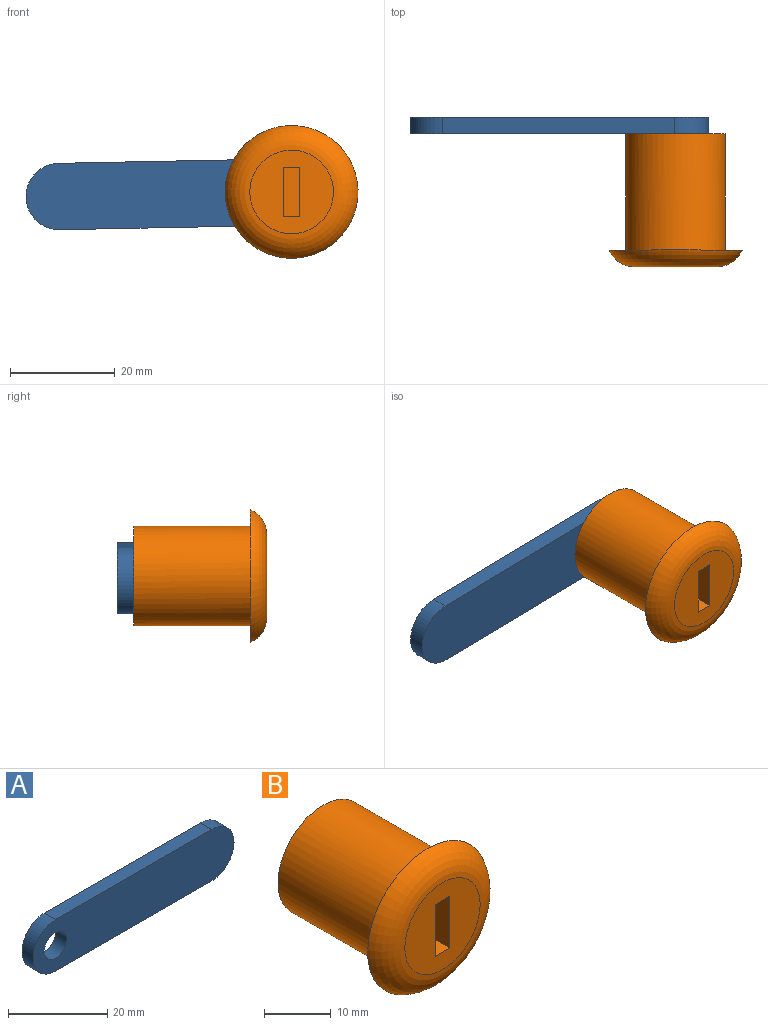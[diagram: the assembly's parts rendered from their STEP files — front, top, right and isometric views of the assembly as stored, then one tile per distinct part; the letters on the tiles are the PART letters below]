
ASSEMBLY  parts=2 mates=1
PART A: 7 faces, bbox 57.2x3.2x12.7 mm
  f0: plane 44.45x3.18mm, normal (0,0,-1), area 141.1mm2, adj f1,f4,f5,f6
  f1: cylinder r=6.35mm len=12.7mm, axis (0,1,0), area 63.3mm2, adj f0,f2,f5,f6
  f2: plane 44.45x3.18mm, normal (0,0,1), area 141.1mm2, adj f1,f4,f5,f6
  f3: cylinder r=3.17mm len=6.35mm, axis (0,1,0), area 63.3mm2, adj f5,f6
  f4: cylinder r=6.35mm len=12.7mm, axis (0,1,0), area 63.3mm2, adj f0,f2,f5,f6
  f5: plane 57.15x12.7mm, normal (0,-1,0), area 659.5mm2, adj f0,f1,f2,f3,f4
  f6: plane 57.15x12.7mm, normal (0,1,0), area 659.5mm2, adj f0,f1,f2,f3,f4
PART B: 10 faces, bbox 28.3x25.4x28.3 mm
  f0: plane 15.98x15.98mm, normal (0,-1,0), area 170.4mm2, adj f2,f5,f6,f7,f8
  f1: plane 25.4x25.4mm, normal (0,1,0), area 221.7mm2, adj f2,f3
  f2: torus R=7.99mm, axis (0,1,0), area 403.9mm2, adj f0,f1
  f3: cylinder r=9.53mm len=22.23mm, axis (0,-1,0), area 1330.1mm2, adj f1,f4
  f4: plane 19.05x19.05mm, normal (0,1,0), area 285mm2, adj f3
  f5: plane 9.53x6.35mm, normal (1,0,0), area 60.5mm2, adj f0,f6,f8,f9
  f6: plane 6.35x3.18mm, normal (0,0,1), area 20.2mm2, adj f0,f5,f7,f9
  f7: plane 9.53x6.35mm, normal (-1,0,0), area 60.5mm2, adj f0,f6,f8,f9
  f8: plane 6.35x3.18mm, normal (0,0,-1), area 20.2mm2, adj f0,f5,f7,f9
  f9: plane 9.53x3.18mm, normal (0,-1,0), area 30.2mm2, adj f5,f6,f7,f8
PLACE A rot(axis=(0,1,0),178.9deg) t=(-0.13,28.57,6.35)mm
PLACE B t=(0,3.18,0)mm
MATE revolute B.f3 <-> A.f4  axis (0,1,0) through (0,25.4,0)mm
